# Revit family: LUXI_PANEL LIGHT_IP
name_source: partatom
category: Apparecchi per illuminazione
revit_build: Autodesk Revit 2016 (Build: 20161004_0715(x64)
units: mm (PartAtom-declared; Revit-internal decimal feet)

## family parameters
Condiviso = No
Host = Superficie
Numero OmniClass = 23.80.70.00
Punto di calcolo locali = Sì
Quota connettore circolare = Usa diametro
Sorgente d'illuminazione = Sì
Taglio con vuoti quando caricato = No
Tipo di parte = Normale
Titolo OmniClass = Lighting

## types (1)
- LPIP036660W840D
    Alimentatore = Incluso, dimmerabile
    Alimentazione = 220-240V AC / 50-60 Hz
    Angolo inclinazione = -90.00°
    Articolo = LPIP036660W840D
    Carico apparente = 36 VA
    Certificazioni = CE / RohS
    Classe di efficienza energetica = A+
    Classe di protezione = II
    Classe di rischio fotobiologico = Esente (RG0)
    Colore = Bianco
    Descrizione = LED panel, elevato grado di protezione
    Dimensioni = 595x595x15
    Emetti da larghezza rettangolo = 519 mm  [stored 1.70276 ft]
    Emetti da lunghezza rettangolo = 519 mm  [stored 1.70276 ft]
    Fattore di correzione di potenza = ≥0,95 (typ.)
    File diagramma fotometrico = LPIP036660W840D Luxi Serie IP 36W 595x595 4000K IP65.IES
    Filtro dei colori = 16777215
    Garanzia = 5 anni
    Grado di protezione = IP65
    H = 15 mm  [stored 0.0492126 ft]
    IFCExportAs = IFCLightFixtureType
    Indice di resa cromatica = ≥80 (typ.)
    Larghezza = 595 mm  [stored 1.9521 ft]
    Lunghezza = 595 mm  [stored 1.9521 ft]
    Masterformat 2016 Codice = 26.50.00
    Masterformat 2016 Descrizione = Lighting
    Materiale 1 = Tecnopolimero Opale Alta Trasmittanza
    Materiale 2 = Alluminio Estruso_Bianco
    Materiale 3 = Lamiera Acciaio
    Modello = Serie IP | Panel Light
    OFF1 = 38 mm  [stored 0.124672 ft]
    OFF2 = 4 mm  [stored 0.0131234 ft]
    OFF3 = 11 mm  [stored 0.0360892 ft]
    Ottiche = Pannello diffondente opalino
    Peso = 3.20 kg
    Potenza = 36 W
    Produttore = Luxi Illuminazione S.r.l.
    Prospetto di default = 2000 mm  [stored 6.56168 ft]
    Protezione agli urti = IK06 (1 Joule)
    Regolazione del flusso luminoso = 1-10V / DALI / PUSH DIM
    Rendi la forma visibile nel rendering = No
    Revisione = 3
    Sistema di illuminazione = Luce indiretta (edge light)
    Sorgente = LED SMD
    Step MacAdam (SDCM) = <4
    Temperatura di esercizio = 0°C / +40°C
    Tipologie di installazione = Incasso / plafone / sospensione
    URL = https://www.luxi.lighting
    Uniclass 2015 Codice = EF_70_80
    Uniclass 2015 Descrizione = Lighting
    Variazione temperatura colore lampada con luminosità attenuata = <Nessuno>
    Vita utile = L70B20 60.000ore

note: [stored X ft] marks values corroborated as IEEE doubles in the binary element streams (Revit-internal decimal feet)
